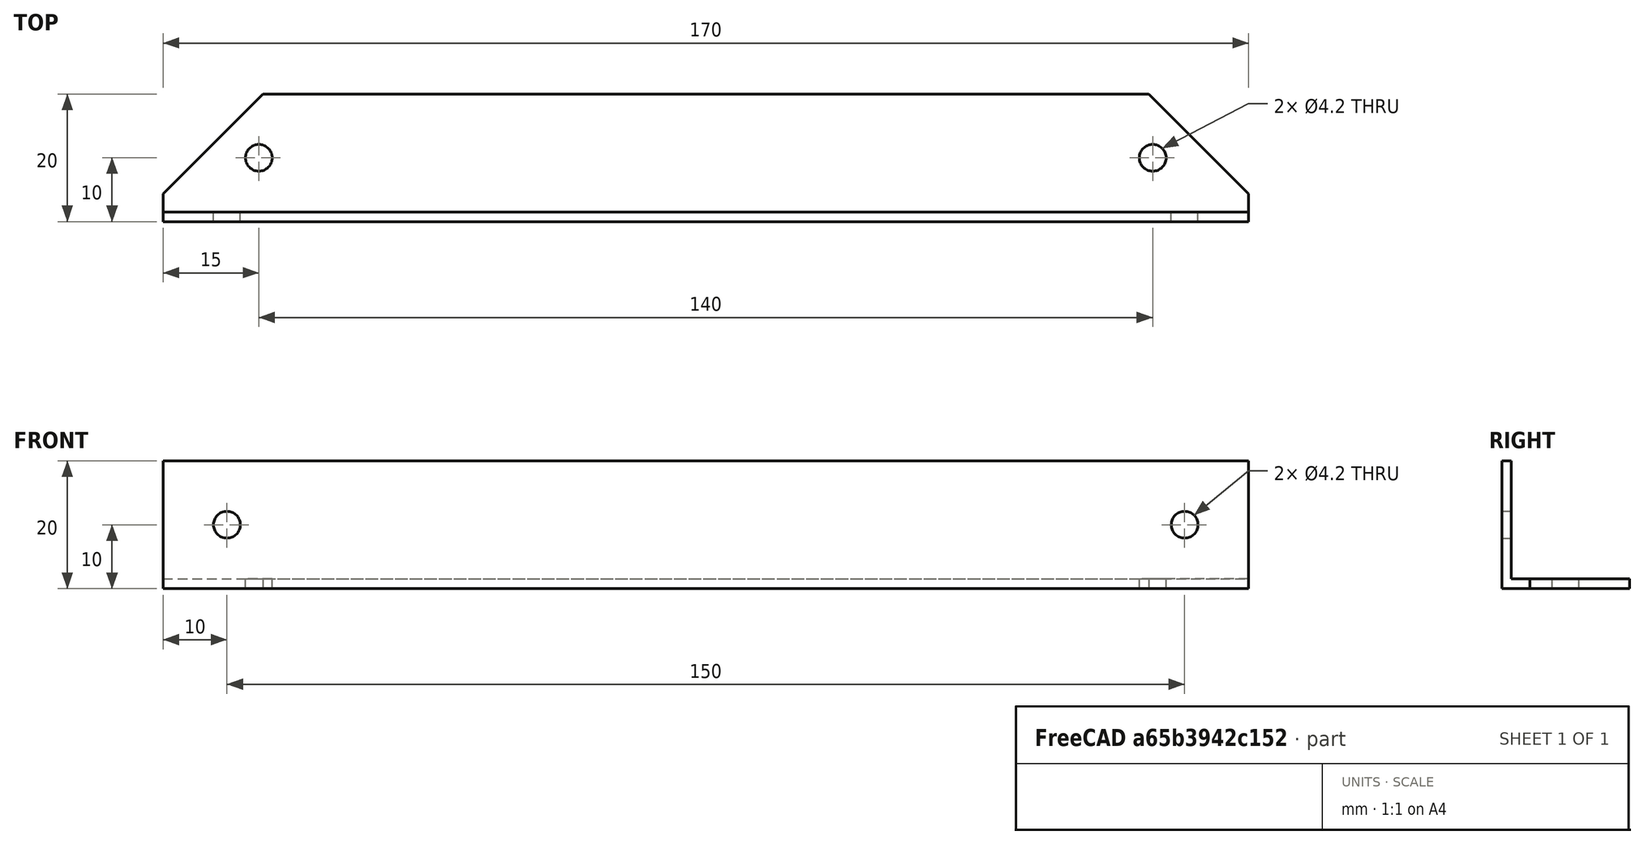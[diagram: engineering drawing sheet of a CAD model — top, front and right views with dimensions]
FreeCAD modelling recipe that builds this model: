
FCSTD DOCUMENT  (FreeCAD 1.0R39319 (Git))
Label: OCT-LBRAC-AA
License: All rights reserved
LicenseURL: https://en.wikipedia.org/wiki/All_rights_reserved
objects: TechDraw::DrawViewDimension×15, Sketcher::SketchObject×4, TechDraw::DrawProjGroupItem×3, PartDesign::Hole×2, PartDesign::Pad×1, PartDesign::Pocket×1, App::VarSet×1, PartDesign::Mirrored×1, PartDesign::Body×1, TechDraw::DrawSVGTemplate×1, TechDraw::DrawProjGroup×1, TechDraw::DrawPage×1
note: 49 computed .brp shape members not serialized (recipe doc carries the construction recipe); baked Part::Feature solids carry a one-line shape summary decoded from their .brp

FEATURE [Sketcher::SketchObject] Sketch
  ArcFitTolerance = 1e-06
  AttachmentSupport = -> [YZ_Plane]
  FullyConstrained = true
  MakeInternals = false
  MapMode = 5
  Placement = pos=(0,0,0) rot=(0.57735,0.57735,0.57735;2.0944rad)
  sketch-geometry (6):
    g0: LineSegment StartX=0 StartY=0 StartZ=0 EndX=20 EndY=0 EndZ=0
    g1: LineSegment StartX=20 StartY=0 StartZ=0 EndX=20 EndY=1.5 EndZ=0
    g2: LineSegment StartX=20 StartY=1.5 StartZ=0 EndX=1.5 EndY=1.5 EndZ=0
    g3: LineSegment StartX=1.5 StartY=1.5 StartZ=0 EndX=1.5 EndY=20 EndZ=0
    g4: LineSegment StartX=1.5 StartY=20 StartZ=0 EndX=0 EndY=20 EndZ=0
    g5: LineSegment StartX=0 StartY=20 StartZ=0 EndX=0 EndY=0 EndZ=0
  constraints (17):
    c: Coincident(g-1,g0)
    c: PointOnObject(g0,g-1)
    c: Coincident(g0,g1)
    c: Coincident(g1,g2)
    c: Horizontal(g2)
    c: Coincident(g2,g3)
    c: Coincident(g3,g4)
    c: PointOnObject(g4,g-2)
    c: Coincident(g4,g5)
    c: Coincident(g5,g0)
    c: Vertical(g1)
    c: Vertical(g3)
    c: Horizontal(g4)
    c: Equal(g4,g1)
    c: DistanceX(g0,g0) = 20
    c: Equal(g0,g5)
    c: DistanceY(g1,g1) = 1.5
FEATURE [PartDesign::Pad] Pad
  Direction = (1,0,0)
  Length = 170
  Length2 = 10
  Midplane = true
  Placement = pos=(0,0,0) rot=(1,1,1;2.0944rad)
  Profile = -> Sketch
  ReferenceAxis = -> Sketch [N_Axis]
  Refine = true
  Suppressed = false
  Type = 0
FEATURE [Sketcher::SketchObject] Sketch002
  ArcFitTolerance = 1e-06
  AttachmentSupport = -> [XZ_Plane]
  FullyConstrained = true
  MakeInternals = false
  MapMode = 5
  Placement = pos=(0,0,0) rot=(1,0,0;1.5708rad)
  sketch-geometry (2):
    g0: Circle CenterX=-75 CenterY=10 CenterZ=0 NormalX=0 NormalY=0 NormalZ=1 AngleXU=0 Radius=2.5
    g1: Circle CenterX=75 CenterY=10 CenterZ=0 NormalX=0 NormalY=0 NormalZ=1 AngleXU=0 Radius=2.5
  constraints (5):
    c: Symmetric(g0,g1,g-2)
    c: DistanceY(g-1,g0) = 10
    c: DistanceX(g0,g1) = 150
    c: Diameter(g0) = 5
    c: Equal(g1,g0)
FEATURE [PartDesign::Hole] Hole  label="panel holes"
  BaseFeature = -> Pad
  CustomThreadClearance = 0
  Depth = 348.12
  DepthType = 1
  Diameter = 4.2
  DrillForDepth = false
  DrillPoint = 1
  DrillPointAngle = 118
  HoleCutCountersinkAngle = 90
  HoleCutCustomValues = false
  HoleCutDepth = 0
  HoleCutDiameter = 6.1
  HoleCutType = 0
  ModelThread = false
  Placement = pos=(0,0,0) rot=(1,1,1;2.0944rad)
  Profile = -> Sketch002
  Refine = true
  Suppressed = false
  Tapered = false
  TaperedAngle = 90
  ThreadClass = 0
  ThreadDepth = 348.12
  ThreadDepthType = 0
  ThreadDirection = 0
  ThreadFit = 0
  ThreadSize = 0
  ThreadType = 0
  Threaded = false
  UseCustomThreadClearance = false
FEATURE [Sketcher::SketchObject] Sketch003
  ArcFitTolerance = 1e-06
  AttachmentSupport = -> [XY_Plane]
  FullyConstrained = true
  MakeInternals = false
  MapMode = 5
  sketch-geometry (2):
    g0: Circle CenterX=-70 CenterY=10 CenterZ=0 NormalX=0 NormalY=0 NormalZ=1 AngleXU=0 Radius=2.5
    g1: Circle CenterX=70 CenterY=10 CenterZ=0 NormalX=0 NormalY=0 NormalZ=1 AngleXU=0 Radius=2.5
  constraints (5):
    c: Symmetric(g1,g0,g-2)
    c: DistanceX(g0,g1) = 140
    c: Equal(g0,g1)
    c: Diameter(g1) = 5
    c: Distance(g1,g-1) = 10
FEATURE [PartDesign::Hole] Hole001  label="base holes"
  BaseFeature = -> Hole
  CustomThreadClearance = 0
  Depth = 348.12
  DepthType = 1
  Diameter = 4.2
  DrillForDepth = false
  DrillPoint = 1
  DrillPointAngle = 118
  HoleCutCountersinkAngle = 90
  HoleCutCustomValues = false
  HoleCutDepth = 0
  HoleCutDiameter = 6.1
  HoleCutType = 0
  ModelThread = false
  Placement = pos=(0,0,0) rot=(1,1,1;2.0944rad)
  Profile = -> Sketch003
  Refine = true
  Reversed = true
  Suppressed = false
  Tapered = false
  TaperedAngle = 90
  ThreadClass = 0
  ThreadDepth = 348.12
  ThreadDepthType = 0
  ThreadDirection = 0
  ThreadFit = 1
  ThreadSize = 0
  ThreadType = 0
  Threaded = false
  UseCustomThreadClearance = false
FEATURE [Sketcher::SketchObject] Sketch004
  ArcFitTolerance = 1e-06
  AttachmentSupport = -> [XY_Plane]
  FullyConstrained = false
  MakeInternals = false
  MapMode = 5
  expr: Constraints[23] = <<dims>>.octWidth
  sketch-geometry (18):
    g0: LineSegment [constr] StartX=87.3991 StartY=0 StartZ=0 EndX=211 EndY=123.601 EndZ=0
    g1: LineSegment [constr] StartX=211 StartY=123.601 StartZ=0 EndX=211 EndY=298.399 EndZ=0
    g2: LineSegment [constr] StartX=211 StartY=298.399 StartZ=0 EndX=87.3991 EndY=422 EndZ=0
    g3: LineSegment [constr] StartX=87.3991 StartY=422 StartZ=0 EndX=-87.3991 EndY=422 EndZ=0
    g4: LineSegment [constr] StartX=-87.3991 StartY=422 StartZ=0 EndX=-211 EndY=298.399 EndZ=0
    g5: LineSegment [constr] StartX=-211 StartY=298.399 StartZ=0 EndX=-211 EndY=123.601 EndZ=0
    g6: LineSegment [constr] StartX=-211 StartY=123.601 StartZ=0 EndX=-87.3991 EndY=0 EndZ=0
    g7: LineSegment [constr] StartX=-87.3991 StartY=0 StartZ=0 EndX=87.3991 EndY=0 EndZ=0
    g8: Circle [constr] CenterX=-1.74e-14 CenterY=211 CenterZ=0 NormalX=0 NormalY=0 NormalZ=1 AngleXU=0 Radius=228.385
    g9: LineSegment [constr] StartX=-209.304 StartY=121.905 StartZ=0 EndX=-181.318 EndY=149.891 EndZ=0
    g10: LineSegment [constr] StartX=-181.318 StartY=149.891 StartZ=0 EndX=-61.1095 EndY=29.6824 EndZ=0
    g11: LineSegment [constr] StartX=-61.1095 StartY=29.6824 StartZ=0 EndX=-89.0955 EndY=1.69639 EndZ=0
    g12: LineSegment StartX=-85 StartY=4.37763 StartZ=0 EndX=-49.3776 EndY=40 EndZ=0
    g13: LineSegment StartX=-49.3776 StartY=40 StartZ=0 EndX=-85 EndY=40 EndZ=0
    g14: LineSegment StartX=-85 StartY=4.37763 StartZ=0 EndX=-85 EndY=40 EndZ=0
    g15: LineSegment [constr] StartX=-1.74e-14 StartY=211 StartZ=0 EndX=-149.2 EndY=61.8005 EndZ=0
    g16: LineSegment [constr] StartX=-85 StartY=4.37763 StartZ=0 EndX=-85 EndY=0 EndZ=0
    g17: LineSegment [constr] StartX=-85 StartY=4.37763 StartZ=0 EndX=-85.7071 EndY=5.08474 EndZ=0
  constraints (46):
    c: Coincident(g0,g1)
    c: Coincident(g1,g2)
    c: Coincident(g2,g3)
    c: Coincident(g3,g4)
    c: Coincident(g4,g5)
    c: Coincident(g5,g6)
    c: Coincident(g6,g7)
    c: Coincident(g7,g0)
    c: Equal(g0, g1-g7) x7
    c: PointOnObject(g0,g8)
    c: PointOnObject(g1,g8)
    c: PointOnObject(g2,g8)
    c: PointOnObject(g3,g8)
    c: PointOnObject(g4,g8)
    c: PointOnObject(g5,g8)
    c: PointOnObject(g6,g8)
    c: PointOnObject(g7,g8)
    c: DistanceY(g6,g3) = 422
    c: Symmetric(g6,g0,g-2)
    c: PointOnObject(g0,g-1)
    c: Coincident(g9,g10)
    c: PointOnObject(g11,g6)
    c: Coincident(g13,g12)
    c: Horizontal(g13)
    c: Coincident(g14,g13)
    c: Vertical(g14)
    c: Equal(g14,g13)
    c: Perpendicular(g6,g11)
    c: Parallel(g10,g6)
    c: Coincident(g15,g8)
    c: PointOnObject(g15,g6)
    c: Coincident(g16,g12)
    c: PointOnObject(g16,g7)
    c: Vertical(g16)
    c: Coincident(g14,g12)
    c: DistanceX(g16,g-1) = 85
    c: DistanceY(g16,g13) = 40
    c: Coincident(g17,g12)
    c: PointOnObject(g17,g11)
    c: Perpendicular(g12,g17)
    c: Distance(g17,g17) = 1
    c: Coincident(g10,g11)
    c: PointOnObject(g9,g6)
    c: Perpendicular(g10,g9)
    c: Distance(g10,g10) = 170
    c: Symmetric(g11,g9,g15)
FEATURE [PartDesign::Pocket] Pocket
  BaseFeature = -> Hole001
  Direction = (0,0,-1)
  Length = 5
  Length2 = 5
  Placement = pos=(0,0,0) rot=(1,1,1;2.0944rad)
  Profile = -> Sketch004
  ReferenceAxis = -> Sketch004 [N_Axis]
  Refine = true
  Reversed = true
  Suppressed = false
  Type = 1
FEATURE [App::VarSet] VarSet  label="dims"
  dims = 0
  octWidth = 422
FEATURE [PartDesign::Mirrored] Mirrored
  BaseFeature = -> Pocket
  MirrorPlane = -> YZ_Plane
  Originals = -> [Pocket]
  Placement = pos=(0,0,0) rot=(1,1,1;2.0944rad)
  Suppressed = false
  TransformMode = 0
FEATURE [PartDesign::Body] Body  label="OCT-LBRAC-AA"
  AllowCompound = false
  Group = -> [Sketch,Pad,Sketch002,Hole,Sketch003,Hole001,Sketch004,Pocket,Mirrored]
  Origin = -> Origin
  Tip = -> Mirrored
FEATURE [TechDraw::DrawSVGTemplate] Template
  EditableTexts = approval_person=S Aphelion; creator=M. Stoll; date_of_issue=07/02/2026; document_status=Released; document_type=OCT-LBRAC-AA; drawing_number=DN; general_tolerances=+- 0.1 mm; language_code=EN; part_material=Aluminium; responsible_department=RD; revision_index=A; scale=1 : 1; sheet_number=1 / 1; supplementary_title_1=Frame Lower Bracket; title=OCT-LBRAC-AA
  Height = 297
  Orientation = 1
  Template = C:/Program Files/FreeCAD 1.0/data/Mod/TechDraw/Templates/A3_Landscape_ISO5457_advanced.svg
  Width = 420
FEATURE [TechDraw::DrawProjGroupItem] View  label="Bottom"
  CoarseView = false
  Direction = (0,0,-1)
  Focus = 100
  HardHidden = false
  IsoCount = 0
  IsoHidden = false
  IsoVisible = false
  LockPosition = true
  Perspective = false
  Rotation = 0
  RotationVector = (1,0,0)
  ScaleType = 2
  ScrubCount = 1
  SeamHidden = false
  SeamVisible = false
  SmoothHidden = false
  SmoothVisible = true
  Source = -> [Mirrored]
  Type = 5
  X = 0
  XDirection = (-1,1e-16,0)
  Y = 0
FEATURE [TechDraw::DrawProjGroupItem] ProjItem  label="Left"
  CoarseView = false
  Direction = (-1,1e-16,-1e-16)
  Focus = 100
  HardHidden = false
  IsoCount = 0
  IsoHidden = false
  IsoVisible = false
  LockPosition = true
  Perspective = false
  Rotation = 0
  RotationVector = (1,0,0)
  ScaleType = 0
  ScrubCount = 1
  SeamHidden = false
  SeamVisible = false
  SmoothHidden = false
  SmoothVisible = true
  Source = -> [Mirrored]
  Type = 2
  X = 133.97
  XDirection = (-1e-16,0,1)
  Y = 0
FEATURE [TechDraw::DrawProjGroupItem] ProjItem001  label="Rear"
  CoarseView = false
  Direction = (1e-16,1,0)
  Focus = 100
  HardHidden = false
  IsoCount = 0
  IsoHidden = false
  IsoVisible = false
  LockPosition = true
  Perspective = false
  Rotation = 0
  RotationVector = (1,0,0)
  ScaleType = 0
  ScrubCount = 1
  SeamHidden = false
  SeamVisible = false
  SmoothHidden = false
  SmoothVisible = true
  Source = -> [Mirrored]
  Type = 4
  X = 0
  XDirection = (-1,1e-16,0)
  Y = 82.9398
FEATURE [TechDraw::DrawProjGroup] ProjGroup
  Anchor = -> View
  AutoDistribute = true
  LockPosition = false
  ProjectionType = 1
  Rotation = 0
  ScaleType = 0
  Source = -> [Mirrored]
  Views = -> [View,ProjItem,ProjItem001]
  X = 196.343
  Y = 126.395
  spacingX = 15
  spacingY = 15
FEATURE [TechDraw::DrawViewDimension] Dimension001
  AngleOverride = false
  Arbitrary = false
  ArbitraryTolerances = false
  BoxCorners = (2) [(-85,-10,0),(85,10,0)]
  EqualTolerance = true
  ExtensionAngle = 0
  FormatSpec = %.2w
  FormatSpecOverTolerance = %+.2w
  FormatSpecUnderTolerance = %+.2w
  Inverted = false
  LineAngle = 0
  LockPosition = false
  MeasureType = 1
  OverTolerance = 0
  References2D = -> [View]
  Rotation = 0
  ScaleType = 0
  TheoreticalExact = false
  Type = 2
  UnderTolerance = 0
  X = -126.367
  Y = 0
FEATURE [TechDraw::DrawViewDimension] Dimension002
  AngleOverride = false
  Arbitrary = false
  ArbitraryTolerances = false
  BoxCorners = (2) [(-85,-10,0),(85,10,0)]
  EqualTolerance = true
  ExtensionAngle = 0
  FormatSpec = ⌀%.2w
  FormatSpecOverTolerance = %+.2w
  FormatSpecUnderTolerance = %+.2w
  Inverted = false
  LineAngle = 0
  LockPosition = false
  MeasureType = 1
  OverTolerance = 0
  References2D = -> [View]
  Rotation = 0
  ScaleType = 0
  TheoreticalExact = false
  Type = 5
  UnderTolerance = 0
  X = -91.1715
  Y = 34.026
FEATURE [TechDraw::DrawViewDimension] Dimension003
  AngleOverride = false
  Arbitrary = false
  ArbitraryTolerances = false
  BoxCorners = (2) [(-85,-10,0),(85,10,0)]
  EqualTolerance = true
  ExtensionAngle = 0
  FormatSpec = %.2w
  FormatSpecOverTolerance = %+.2w
  FormatSpecUnderTolerance = %+.2w
  Inverted = false
  LineAngle = 0
  LockPosition = false
  MeasureType = 1
  OverTolerance = 0
  References2D = -> [ProjItem001]
  Rotation = 0
  ScaleType = 0
  TheoreticalExact = false
  Type = 2
  UnderTolerance = 0
  X = -128.054
  Y = 0
FEATURE [TechDraw::DrawViewDimension] Dimension006
  AngleOverride = false
  Arbitrary = false
  ArbitraryTolerances = false
  BoxCorners = (2) [(-85,-10,0),(85,10,0)]
  EqualTolerance = true
  ExtensionAngle = 0
  FormatSpec = %.1f
  FormatSpecOverTolerance = %+.2w
  FormatSpecUnderTolerance = %+.2w
  Inverted = false
  LineAngle = 0
  LockPosition = false
  MeasureType = 1
  OverTolerance = 0
  References2D = -> [View]
  Rotation = 0
  ScaleType = 0
  TheoreticalExact = false
  Type = 0
  UnderTolerance = 0
  X = -110.654
  Y = 0.570219
FEATURE [TechDraw::DrawViewDimension] Dimension007
  AngleOverride = false
  Arbitrary = false
  ArbitraryTolerances = false
  BoxCorners = (2) [(-85,-10,0),(85,10,0)]
  EqualTolerance = true
  ExtensionAngle = 0
  FormatSpec = ⌀%.2w
  FormatSpecOverTolerance = %+.2w
  FormatSpecUnderTolerance = %+.2w
  Inverted = false
  LineAngle = 0
  LockPosition = false
  MeasureType = 1
  OverTolerance = 0
  References2D = -> [ProjItem001]
  Rotation = 0
  ScaleType = 0
  TheoreticalExact = false
  Type = 5
  UnderTolerance = 0
  X = -96.6991
  Y = 40.3633
FEATURE [TechDraw::DrawViewDimension] Dimension010
  AngleOverride = false
  Arbitrary = false
  ArbitraryTolerances = false
  BoxCorners = (2) [(-85,-10,0),(85,10,0)]
  EqualTolerance = true
  ExtensionAngle = 0
  FormatSpec = %.2w
  FormatSpecOverTolerance = %+.2w
  FormatSpecUnderTolerance = %+.2w
  Inverted = false
  LineAngle = 0
  LockPosition = false
  MeasureType = 1
  OverTolerance = 0
  References2D = -> [View]
  Rotation = 0
  ScaleType = 0
  TheoreticalExact = false
  Type = 6
  UnderTolerance = 0
  X = 94.4627
  Y = 13.9022
FEATURE [TechDraw::DrawViewDimension] Dimension011
  AngleOverride = false
  Arbitrary = false
  ArbitraryTolerances = false
  BoxCorners = (2) [(-10,-10,0),(10,10,0)]
  EqualTolerance = true
  ExtensionAngle = 0
  FormatSpec = %.2f
  FormatSpecOverTolerance = %+.2f
  FormatSpecUnderTolerance = %+.2f
  Inverted = false
  LineAngle = 0
  LockPosition = false
  MeasureType = 1
  OverTolerance = 0
  References2D = -> [ProjItem]
  Rotation = 0
  ScaleType = 0
  TheoreticalExact = false
  Type = 0
  UnderTolerance = 0
  X = 23.2402
  Y = -0.158216
FEATURE [TechDraw::DrawViewDimension] Dimension012
  AngleOverride = false
  Arbitrary = false
  ArbitraryTolerances = false
  BoxCorners = (2) [(-10,-10,0),(10,10,0)]
  EqualTolerance = true
  ExtensionAngle = 0
  FormatSpec = %.2f
  FormatSpecOverTolerance = %+.2f
  FormatSpecUnderTolerance = %+.2f
  Inverted = false
  LineAngle = 0
  LockPosition = false
  MeasureType = 1
  OverTolerance = 0
  References2D = -> [ProjItem]
  Rotation = 0
  ScaleType = 0
  TheoreticalExact = false
  Type = 0
  UnderTolerance = 0
  X = 1.21301
  Y = 27.4035
FEATURE [TechDraw::DrawViewDimension] Dimension013
  AngleOverride = false
  Arbitrary = false
  ArbitraryTolerances = false
  BoxCorners = (2) [(-85,-10,0),(85,10,0)]
  EqualTolerance = true
  ExtensionAngle = 0
  FormatSpec = %.1f
  FormatSpecOverTolerance = %+.2f
  FormatSpecUnderTolerance = %+.2f
  Inverted = false
  LineAngle = 0
  LockPosition = false
  MeasureType = 1
  OverTolerance = 0
  References2D = -> [ProjItem001]
  Rotation = 0
  ScaleType = 0
  TheoreticalExact = false
  Type = 0
  UnderTolerance = 0
  X = 92.1656
  Y = -18.4923
FEATURE [TechDraw::DrawViewDimension] Dimension014
  AngleOverride = false
  Arbitrary = false
  ArbitraryTolerances = false
  BoxCorners = (2) [(-85,-10,0),(85,10,0)]
  EqualTolerance = true
  ExtensionAngle = 0
  FormatSpec = %.1f
  FormatSpecOverTolerance = %+.2f
  FormatSpecUnderTolerance = %+.2f
  Inverted = false
  LineAngle = 0
  LockPosition = false
  MeasureType = 1
  OverTolerance = 0
  References2D = -> [View]
  Rotation = 0
  ScaleType = 0
  TheoreticalExact = false
  Type = 0
  UnderTolerance = 0
  X = 114.297
  Y = -21.4763
FEATURE [TechDraw::DrawViewDimension] Dimension015
  AngleOverride = false
  Arbitrary = false
  ArbitraryTolerances = false
  BoxCorners = (2) [(-85,-10,0),(85,10,0)]
  EqualTolerance = true
  ExtensionAngle = 0
  FormatSpec = %.1f
  FormatSpecOverTolerance = %+.2f
  FormatSpecUnderTolerance = %+.2f
  Inverted = false
  LineAngle = 0
  LockPosition = false
  MeasureType = 1
  OverTolerance = 0
  References2D = -> [ProjItem001]
  Rotation = 0
  ScaleType = 0
  TheoreticalExact = false
  Type = 0
  UnderTolerance = 0
  X = -80
  Y = 35.6475
FEATURE [TechDraw::DrawViewDimension] Dimension016
  AngleOverride = false
  Arbitrary = false
  ArbitraryTolerances = false
  BoxCorners = (2) [(-85,-10,0),(85,10,0)]
  EqualTolerance = true
  ExtensionAngle = 0
  FormatSpec = %.1f
  FormatSpecOverTolerance = %+.2f
  FormatSpecUnderTolerance = %+.2f
  Inverted = false
  LineAngle = 0
  LockPosition = false
  MeasureType = 1
  OverTolerance = 0
  References2D = -> [ProjItem001]
  Rotation = 0
  ScaleType = 0
  TheoreticalExact = false
  Type = 0
  UnderTolerance = 0
  X = 0
  Y = 35.6475
FEATURE [TechDraw::DrawViewDimension] Dimension
  AngleOverride = false
  Arbitrary = false
  ArbitraryTolerances = false
  BoxCorners = (2) [(-85,-10,0),(85,10,0)]
  EqualTolerance = true
  ExtensionAngle = 0
  FormatSpec = %.1f
  FormatSpecOverTolerance = %+.2f
  FormatSpecUnderTolerance = %+.2f
  Inverted = false
  LineAngle = 0
  LockPosition = false
  MeasureType = 1
  OverTolerance = 0
  References2D = -> [ProjItem001]
  Rotation = 0
  ScaleType = 0
  TheoreticalExact = false
  Type = 0
  UnderTolerance = 0
  X = 0
  Y = -14.9985
FEATURE [TechDraw::DrawViewDimension] Dimension017
  AngleOverride = false
  Arbitrary = false
  ArbitraryTolerances = false
  BoxCorners = (2) [(-85,-10,0),(85,10,0)]
  EqualTolerance = true
  ExtensionAngle = 0
  FormatSpec = %.1f
  FormatSpecOverTolerance = %+.2f
  FormatSpecUnderTolerance = %+.2f
  Inverted = false
  LineAngle = 0
  LockPosition = false
  MeasureType = 1
  OverTolerance = 0
  References2D = -> [View]
  Rotation = 0
  ScaleType = 0
  TheoreticalExact = false
  Type = 1
  UnderTolerance = 0
  X = -77.5
  Y = -16.1195
FEATURE [TechDraw::DrawViewDimension] Dimension018
  AngleOverride = false
  Arbitrary = false
  ArbitraryTolerances = false
  BoxCorners = (2) [(-85,-10,0),(85,10,0)]
  EqualTolerance = true
  ExtensionAngle = 0
  FormatSpec = %.1f
  FormatSpecOverTolerance = %+.2f
  FormatSpecUnderTolerance = %+.2f
  Inverted = false
  LineAngle = 0
  LockPosition = false
  MeasureType = 1
  OverTolerance = 0
  References2D = -> [View]
  Rotation = 0
  ScaleType = 0
  TheoreticalExact = false
  Type = 0
  UnderTolerance = 0
  X = 0
  Y = -16.1195
FEATURE [TechDraw::DrawPage] Page
  KeepUpdated = true
  NextBalloonIndex = 1
  ProjectionType = 1
  Template = -> Template
  Views = -> [ProjGroup,Dimension001,Dimension002,Dimension003,Dimension006,Dimension007,Dimension010,Dimension011,Dimension012,Dimension013,Dimension014,Dimension015,Dimension016,Dimension,Dimension017,Dimension018]
